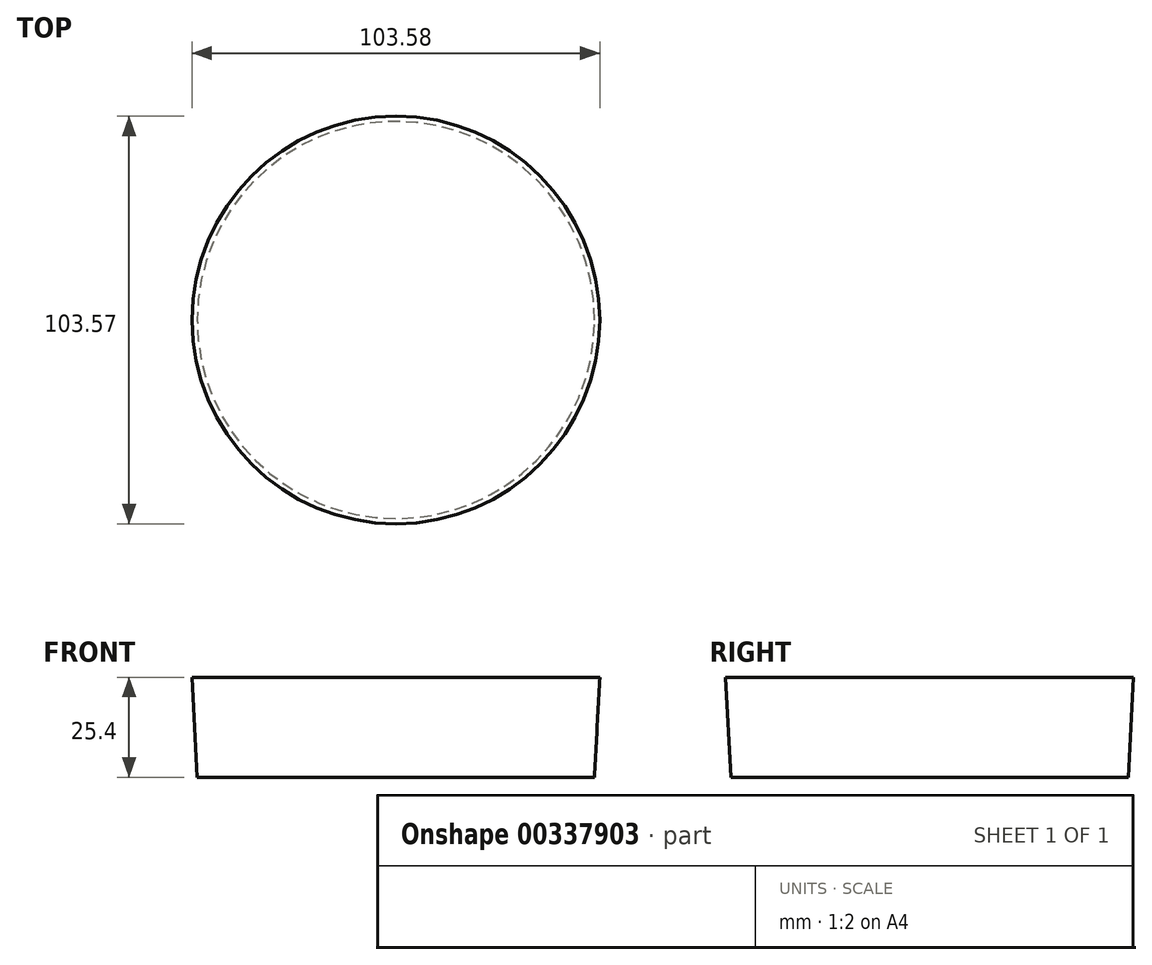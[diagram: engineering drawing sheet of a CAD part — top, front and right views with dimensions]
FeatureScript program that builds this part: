
annotation { "Feature Type Name" : "Feature", "Feature Type Description" : "" }
export const myFeature = defineFeature(function(context is Context, id is Id, definition is map)
    precondition{}
    {
        {
            var Q0;
            Q0=qCreatedBy(makeId("Top.planeOp"),FACE);
            var sketch = newSketch(context, id + "F0", { "sketchPlane" : qUnion([Q0])});
            skCircle(sketch, "E0", {"center": v(-0.23, -0.81) * mm, "radius": 50.46 * mm});
            skSolve(sketch);
        }
        {
            var Q0;
            Q0=makeQuery(id+"F0.imprint","IMPRINT",FACE,{"disambiguationData":[TD([[makeQuery(id+"F0.imprint","IMPRINT",EDGE,{"derivedFrom":sQuery(id+"F0.wireOp",EDGE,"E0")}),1.0]])]});
            var Q1;
            Q1 = qSketchRegion(id + "F0", true);
            extrude(context, id + "F1", {"entities" : qUnion([Q0, Q1]), "depth" : 25.4 * mm, "hasDraft" : true, "draftAngle" : 3 * degree});
        }
    });
